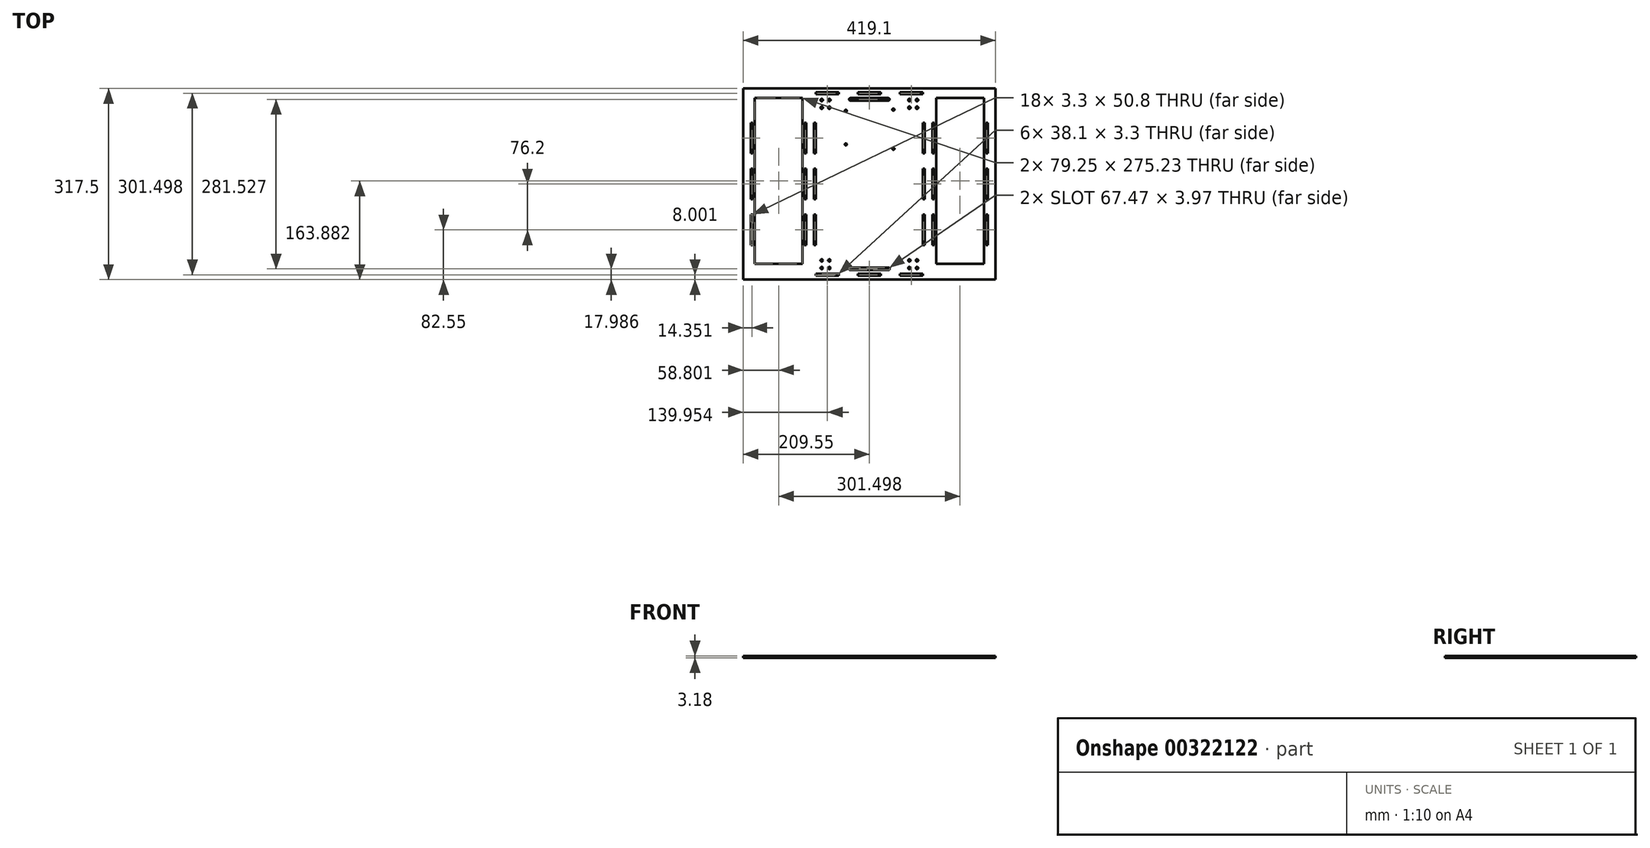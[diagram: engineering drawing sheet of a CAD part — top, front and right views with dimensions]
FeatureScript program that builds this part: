
annotation { "Feature Type Name" : "Feature", "Feature Type Description" : "" }
export const myFeature = defineFeature(function(context is Context, id is Id, definition is map)
    precondition{}
    {
        {
            var Q0;
            Q0=qCreatedBy(makeId("Top.planeOp"),FACE);
            var sketch = newSketch(context, id + "F0", { "sketchPlane" : qUnion([Q0])});
            skLineSegment(sketch, "E0.bottom", {"start": v(111.12, -158.75) * mm, "end": v(-111.12, -158.75) * mm});
            skLineSegment(sketch, "E0.top", {"start": v(111.12, 158.75) * mm, "end": v(-111.12, 158.75) * mm});
            skLineSegment(sketch, "E0.left", {"start": v(111.12, -158.75) * mm, "end": v(111.12, 158.75) * mm, "construction": true});
            skPoint(sketch, "E0.middle", {"position": v(0, 0) * mm});
            skLineSegment(sketch, "E1.bottom", {"start": v(-88.65, 152.4) * mm, "end": v(-50.55, 152.4) * mm});
            skLineSegment(sketch, "E1.top", {"start": v(-88.65, 149.1) * mm, "end": v(-50.55, 149.1) * mm});
            skLineSegment(sketch, "E1.left", {"start": v(-88.65, 152.4) * mm, "end": v(-88.65, 149.1) * mm});
            skLineSegment(sketch, "E1.right", {"start": v(-50.55, 152.4) * mm, "end": v(-50.55, 149.1) * mm});
            skLineSegment(sketch, "E2.bottom", {"start": v(-19.05, 152.4) * mm, "end": v(19.05, 152.4) * mm});
            skLineSegment(sketch, "E2.top", {"start": v(-19.05, 149.1) * mm, "end": v(19.05, 149.1) * mm});
            skLineSegment(sketch, "E2.left", {"start": v(-19.05, 152.4) * mm, "end": v(-19.05, 149.1) * mm});
            skLineSegment(sketch, "E2.right", {"start": v(19.05, 152.4) * mm, "end": v(19.05, 149.1) * mm});
            skLineSegment(sketch, "E3", {"start": v(-50.55, 152.4) * mm, "end": v(-19.05, 152.4) * mm, "construction": true});
            skLineSegment(sketch, "E4.MirrorCS", {"start": v(88.65, 149.1) * mm, "end": v(50.55, 149.1) * mm});
            skLineSegment(sketch, "E5.MirrorCS", {"start": v(88.65, 152.4) * mm, "end": v(50.55, 152.4) * mm});
            skLineSegment(sketch, "E6.MirrorCS", {"start": v(50.55, 152.4) * mm, "end": v(50.55, 149.1) * mm});
            skLineSegment(sketch, "E7.MirrorCS", {"start": v(88.65, 152.4) * mm, "end": v(88.65, 149.1) * mm});
            skLineSegment(sketch, "E8.MirrorCS", {"start": v(-50.55, -152.4) * mm, "end": v(-50.55, -149.1) * mm});
            skLineSegment(sketch, "E9.MirrorCS", {"start": v(-19.05, -149.1) * mm, "end": v(19.05, -149.1) * mm});
            skLineSegment(sketch, "E10.MirrorCS", {"start": v(19.05, -152.4) * mm, "end": v(19.05, -149.1) * mm});
            skLineSegment(sketch, "E11.MirrorCS", {"start": v(88.65, -149.1) * mm, "end": v(50.55, -149.1) * mm});
            skLineSegment(sketch, "E12.MirrorCS", {"start": v(50.55, -152.4) * mm, "end": v(50.55, -149.1) * mm});
            skLineSegment(sketch, "E13.MirrorCS", {"start": v(-88.65, -149.1) * mm, "end": v(-50.55, -149.1) * mm});
            skLineSegment(sketch, "E14.MirrorCS", {"start": v(88.65, -152.4) * mm, "end": v(88.65, -149.1) * mm});
            skLineSegment(sketch, "E15.MirrorCS", {"start": v(-19.05, -152.4) * mm, "end": v(-19.05, -149.1) * mm});
            skLineSegment(sketch, "E16.MirrorCS", {"start": v(88.65, -152.4) * mm, "end": v(50.55, -152.4) * mm});
            skLineSegment(sketch, "E17.MirrorCS", {"start": v(-19.05, -152.4) * mm, "end": v(19.05, -152.4) * mm});
            skLineSegment(sketch, "E18.MirrorCS", {"start": v(-50.55, -152.4) * mm, "end": v(-19.05, -152.4) * mm, "construction": true});
            skLineSegment(sketch, "E19.MirrorCS", {"start": v(-88.65, -152.4) * mm, "end": v(-50.55, -152.4) * mm});
            skLineSegment(sketch, "E20.MirrorCS", {"start": v(-88.65, -152.4) * mm, "end": v(-88.65, -149.1) * mm});
            skLineSegment(sketch, "E21.bottom", {"start": v(-107.95, 101.6) * mm, "end": v(-104.65, 101.6) * mm});
            skLineSegment(sketch, "E21.top", {"start": v(-107.95, 50.8) * mm, "end": v(-104.65, 50.8) * mm});
            skLineSegment(sketch, "E21.left", {"start": v(-107.95, 101.6) * mm, "end": v(-107.95, 50.8) * mm});
            skLineSegment(sketch, "E21.right", {"start": v(-104.65, 101.6) * mm, "end": v(-104.65, 50.8) * mm});
            skLineSegment(sketch, "E22.0.1.0", {"start": v(-104.65, 25.4) * mm, "end": v(-104.65, -25.4) * mm});
            skLineSegment(sketch, "E22.0.1.1", {"start": v(-107.95, 25.4) * mm, "end": v(-107.95, -25.4) * mm});
            skLineSegment(sketch, "E22.0.1.2", {"start": v(-107.95, 25.4) * mm, "end": v(-104.65, 25.4) * mm});
            skLineSegment(sketch, "E22.0.1.3", {"start": v(-107.95, -25.4) * mm, "end": v(-104.65, -25.4) * mm});
            skLineSegment(sketch, "E22.0.2.0", {"start": v(-104.65, -50.8) * mm, "end": v(-104.65, -101.6) * mm});
            skLineSegment(sketch, "E22.0.2.1", {"start": v(-107.95, -50.8) * mm, "end": v(-107.95, -101.6) * mm});
            skLineSegment(sketch, "E22.0.2.2", {"start": v(-107.95, -50.8) * mm, "end": v(-104.65, -50.8) * mm});
            skLineSegment(sketch, "E22.0.2.3", {"start": v(-107.95, -101.6) * mm, "end": v(-104.65, -101.6) * mm});
            skLineSegment(sketch, "E22.direction1", {"start": v(-107.95, 50.8) * mm, "end": v(-91.95, 50.8) * mm, "construction": true});
            skLineSegment(sketch, "E22.direction2", {"start": v(-107.95, 50.8) * mm, "end": v(-107.95, -25.4) * mm, "construction": true});
            skLineSegment(sketch, "E23.MirrorCS", {"start": v(104.65, 25.4) * mm, "end": v(104.65, -25.4) * mm});
            skLineSegment(sketch, "E24.MirrorCS", {"start": v(107.95, -50.8) * mm, "end": v(104.65, -50.8) * mm});
            skLineSegment(sketch, "E25.MirrorCS", {"start": v(107.95, 25.4) * mm, "end": v(107.95, -25.4) * mm});
            skLineSegment(sketch, "E26.MirrorCS", {"start": v(107.95, -101.6) * mm, "end": v(104.65, -101.6) * mm});
            skLineSegment(sketch, "E27.MirrorCS", {"start": v(107.95, 25.4) * mm, "end": v(104.65, 25.4) * mm});
            skLineSegment(sketch, "E28.MirrorCS", {"start": v(107.95, -25.4) * mm, "end": v(104.65, -25.4) * mm});
            skLineSegment(sketch, "E29.MirrorCS", {"start": v(107.95, 50.8) * mm, "end": v(107.95, -25.4) * mm, "construction": true});
            skLineSegment(sketch, "E30.MirrorCS", {"start": v(107.95, 101.6) * mm, "end": v(104.65, 101.6) * mm});
            skLineSegment(sketch, "E31.MirrorCS", {"start": v(107.95, 50.8) * mm, "end": v(104.65, 50.8) * mm});
            skLineSegment(sketch, "E32.MirrorCS", {"start": v(107.95, 101.6) * mm, "end": v(107.95, 50.8) * mm});
            skLineSegment(sketch, "E33.MirrorCS", {"start": v(104.65, -50.8) * mm, "end": v(104.65, -101.6) * mm});
            skLineSegment(sketch, "E34.MirrorCS", {"start": v(104.65, 101.6) * mm, "end": v(104.65, 50.8) * mm});
            skLineSegment(sketch, "E35.MirrorCS", {"start": v(107.95, -50.8) * mm, "end": v(107.95, -101.6) * mm});
            skPoint(sketch, "E36.middle", {"position": v(0, 93.75) * mm});
            skCircle(sketch, "E37", {"center": v(39.92, 123.7) * mm, "radius": 1.75 * mm});
            skCircle(sketch, "E38", {"center": v(39.92, 58.7) * mm, "radius": 1.75 * mm});
            skCircle(sketch, "E39", {"center": v(-39.04, 65.88) * mm, "radius": 1.75 * mm});
            skCircle(sketch, "E40.MirrorC", {"center": v(-39.04, 121.62) * mm, "radius": 1.75 * mm});
            skLineSegment(sketch, "E41.0.1.0", {"start": v(-88.65, 101.6) * mm, "end": v(-88.65, 50.8) * mm});
            skLineSegment(sketch, "E41.3.1.0", {"start": v(-91.95, 101.6) * mm, "end": v(-91.95, 50.8) * mm});
            skLineSegment(sketch, "E41.6.1.0", {"start": v(-91.95, 101.6) * mm, "end": v(-88.65, 101.6) * mm});
            skLineSegment(sketch, "E41.9.1.0", {"start": v(-91.95, 50.8) * mm, "end": v(-88.65, 50.8) * mm});
            skLineSegment(sketch, "E41.0.1.1", {"start": v(-88.65, 25.4) * mm, "end": v(-88.65, -25.4) * mm});
            skLineSegment(sketch, "E41.3.1.1", {"start": v(-91.95, 25.4) * mm, "end": v(-91.95, -25.4) * mm});
            skLineSegment(sketch, "E41.6.1.1", {"start": v(-91.95, 25.4) * mm, "end": v(-88.65, 25.4) * mm});
            skLineSegment(sketch, "E41.9.1.1", {"start": v(-91.95, -25.4) * mm, "end": v(-88.65, -25.4) * mm});
            skLineSegment(sketch, "E41.0.1.2", {"start": v(-88.65, -50.8) * mm, "end": v(-88.65, -101.6) * mm});
            skLineSegment(sketch, "E41.3.1.2", {"start": v(-91.95, -50.8) * mm, "end": v(-91.95, -101.6) * mm});
            skLineSegment(sketch, "E41.6.1.2", {"start": v(-91.95, -50.8) * mm, "end": v(-88.65, -50.8) * mm});
            skLineSegment(sketch, "E41.9.1.2", {"start": v(-91.95, -101.6) * mm, "end": v(-88.65, -101.6) * mm});
            skLineSegment(sketch, "E42.MirrorCS", {"start": v(91.95, 101.6) * mm, "end": v(91.95, 50.8) * mm});
            skLineSegment(sketch, "E43.MirrorCS", {"start": v(91.95, 101.6) * mm, "end": v(88.65, 101.6) * mm});
            skLineSegment(sketch, "E44.MirrorCS", {"start": v(91.95, 50.8) * mm, "end": v(88.65, 50.8) * mm});
            skLineSegment(sketch, "E45.MirrorCS", {"start": v(91.95, -50.8) * mm, "end": v(91.95, -101.6) * mm});
            skLineSegment(sketch, "E46.MirrorCS", {"start": v(88.65, 25.4) * mm, "end": v(88.65, -25.4) * mm});
            skLineSegment(sketch, "E47.MirrorCS", {"start": v(91.95, -50.8) * mm, "end": v(88.65, -50.8) * mm});
            skLineSegment(sketch, "E48.MirrorCS", {"start": v(91.95, 25.4) * mm, "end": v(91.95, -25.4) * mm});
            skLineSegment(sketch, "E49.MirrorCS", {"start": v(91.95, -101.6) * mm, "end": v(88.65, -101.6) * mm});
            skLineSegment(sketch, "E50.MirrorCS", {"start": v(91.95, 25.4) * mm, "end": v(88.65, 25.4) * mm});
            skLineSegment(sketch, "E51.MirrorCS", {"start": v(91.95, -25.4) * mm, "end": v(88.65, -25.4) * mm});
            skLineSegment(sketch, "E52.MirrorCS", {"start": v(88.65, 101.6) * mm, "end": v(88.65, 50.8) * mm});
            skLineSegment(sketch, "E53.MirrorCS", {"start": v(88.65, -50.8) * mm, "end": v(88.65, -101.6) * mm});
            skLineSegment(sketch, "E54", {"start": v(-88.65, 101.6) * mm, "end": v(-88.65, 149.1) * mm, "construction": true});
            skCircle(sketch, "E55", {"center": v(-79.12, 139.57) * mm, "radius": 1.98 * mm});
            skCircle(sketch, "E56", {"center": v(-66.42, 139.57) * mm, "radius": 1.98 * mm});
            skCircle(sketch, "E57", {"center": v(-79.12, 126.87) * mm, "radius": 1.98 * mm});
            skCircle(sketch, "E58", {"center": v(-66.42, 126.87) * mm, "radius": 1.98 * mm});
            skCircle(sketch, "E59.MirrorC", {"center": v(79.12, 126.87) * mm, "radius": 1.98 * mm});
            skCircle(sketch, "E60.MirrorC", {"center": v(79.12, 139.57) * mm, "radius": 1.98 * mm});
            skCircle(sketch, "E61.MirrorC", {"center": v(66.42, 139.57) * mm, "radius": 1.98 * mm});
            skCircle(sketch, "E62.MirrorC", {"center": v(66.42, 126.87) * mm, "radius": 1.98 * mm});
            skCircle(sketch, "E63.MirrorC", {"center": v(-79.12, -139.57) * mm, "radius": 1.98 * mm});
            skCircle(sketch, "E64.MirrorC", {"center": v(-79.12, -126.87) * mm, "radius": 1.98 * mm});
            skCircle(sketch, "E65.MirrorC", {"center": v(-66.42, -139.57) * mm, "radius": 1.98 * mm});
            skCircle(sketch, "E66.MirrorC", {"center": v(-66.42, -126.87) * mm, "radius": 1.98 * mm});
            skCircle(sketch, "E67.MirrorC", {"center": v(66.42, -139.57) * mm, "radius": 1.98 * mm});
            skCircle(sketch, "E68.MirrorC", {"center": v(79.12, -126.87) * mm, "radius": 1.98 * mm});
            skCircle(sketch, "E69.MirrorC", {"center": v(66.42, -126.87) * mm, "radius": 1.98 * mm});
            skCircle(sketch, "E70.MirrorC", {"center": v(79.12, -139.57) * mm, "radius": 1.98 * mm});
            skLineSegment(sketch, "E71.bottom", {"start": v(228.6, -228.6) * mm, "end": v(-228.6, -228.6) * mm, "construction": true});
            skLineSegment(sketch, "E71.top", {"start": v(228.6, 228.6) * mm, "end": v(-228.6, 228.6) * mm, "construction": true});
            skLineSegment(sketch, "E71.left", {"start": v(228.6, -228.6) * mm, "end": v(228.6, 228.6) * mm, "construction": true});
            skLineSegment(sketch, "E71.right", {"start": v(-228.6, -228.6) * mm, "end": v(-228.6, 228.6) * mm, "construction": true});
            skLineSegment(sketch, "E72", {"start": v(111.12, 158.75) * mm, "end": v(209.55, 158.75) * mm});
            skLineSegment(sketch, "E73", {"start": v(209.55, 158.75) * mm, "end": v(209.55, -158.75) * mm});
            skLineSegment(sketch, "E74", {"start": v(209.55, -158.75) * mm, "end": v(111.12, -158.75) * mm});
            skLineSegment(sketch, "E75.bottom", {"start": v(111.12, 142.75) * mm, "end": v(190.37, 142.75) * mm});
            skLineSegment(sketch, "E75.top", {"start": v(111.12, -132.48) * mm, "end": v(190.37, -132.48) * mm});
            skLineSegment(sketch, "E75.left", {"start": v(111.12, 142.75) * mm, "end": v(111.12, -132.48) * mm});
            skLineSegment(sketch, "E75.right", {"start": v(190.37, 142.75) * mm, "end": v(190.37, -132.48) * mm});
            skLineSegment(sketch, "E76.1.0.0", {"start": v(196.85, -25.4) * mm, "end": v(193.55, -25.4) * mm});
            skLineSegment(sketch, "E76.1.0.1", {"start": v(193.55, -50.8) * mm, "end": v(193.55, -101.6) * mm});
            skLineSegment(sketch, "E76.1.0.2", {"start": v(196.85, 101.6) * mm, "end": v(196.85, 50.8) * mm});
            skLineSegment(sketch, "E76.1.0.3", {"start": v(196.85, 50.8) * mm, "end": v(193.55, 50.8) * mm});
            skLineSegment(sketch, "E76.1.0.4", {"start": v(196.85, 25.4) * mm, "end": v(193.55, 25.4) * mm});
            skLineSegment(sketch, "E76.1.0.5", {"start": v(196.85, 50.8) * mm, "end": v(196.85, -25.4) * mm, "construction": true});
            skLineSegment(sketch, "E76.1.0.6", {"start": v(193.55, 25.4) * mm, "end": v(193.55, -25.4) * mm});
            skLineSegment(sketch, "E76.1.0.7", {"start": v(193.55, 101.6) * mm, "end": v(193.55, 50.8) * mm});
            skLineSegment(sketch, "E76.1.0.8", {"start": v(196.85, 25.4) * mm, "end": v(196.85, -25.4) * mm});
            skLineSegment(sketch, "E76.1.0.9", {"start": v(196.85, -50.8) * mm, "end": v(193.55, -50.8) * mm});
            skLineSegment(sketch, "E76.1.0.10", {"start": v(196.85, -101.6) * mm, "end": v(193.55, -101.6) * mm});
            skLineSegment(sketch, "E76.1.0.11", {"start": v(196.85, -50.8) * mm, "end": v(196.85, -101.6) * mm});
            skLineSegment(sketch, "E76.1.0.12", {"start": v(196.85, 101.6) * mm, "end": v(193.55, 101.6) * mm});
            skLineSegment(sketch, "E76.direction1", {"start": v(104.65, -101.6) * mm, "end": v(193.55, -101.6) * mm, "construction": true});
            skLineSegment(sketch, "E77.MirrorCS", {"start": v(-196.85, 50.8) * mm, "end": v(-196.85, -25.4) * mm, "construction": true});
            skLineSegment(sketch, "E78.MirrorCS", {"start": v(-196.85, -101.6) * mm, "end": v(-193.55, -101.6) * mm});
            skLineSegment(sketch, "E79.MirrorCS", {"start": v(-111.12, -158.75) * mm, "end": v(-111.12, 158.75) * mm, "construction": true});
            skLineSegment(sketch, "E80.MirrorCS", {"start": v(-196.85, 101.6) * mm, "end": v(-193.55, 101.6) * mm});
            skLineSegment(sketch, "E81.MirrorCS", {"start": v(-193.55, -50.8) * mm, "end": v(-193.55, -101.6) * mm});
            skLineSegment(sketch, "E82.MirrorCS", {"start": v(-193.55, 101.6) * mm, "end": v(-193.55, 50.8) * mm});
            skLineSegment(sketch, "E83.MirrorCS", {"start": v(-111.12, 158.75) * mm, "end": v(-209.55, 158.75) * mm});
            skLineSegment(sketch, "E84.MirrorCS", {"start": v(-196.85, 50.8) * mm, "end": v(-193.55, 50.8) * mm});
            skLineSegment(sketch, "E85.MirrorCS", {"start": v(-209.55, -158.75) * mm, "end": v(-111.12, -158.75) * mm});
            skLineSegment(sketch, "E86.MirrorCS", {"start": v(-196.85, -50.8) * mm, "end": v(-193.55, -50.8) * mm});
            skLineSegment(sketch, "E87.MirrorCS", {"start": v(-196.85, -50.8) * mm, "end": v(-196.85, -101.6) * mm});
            skLineSegment(sketch, "E88.MirrorCS", {"start": v(-196.85, -25.4) * mm, "end": v(-193.55, -25.4) * mm});
            skLineSegment(sketch, "E89.MirrorCS", {"start": v(-111.12, -132.48) * mm, "end": v(-190.37, -132.48) * mm});
            skLineSegment(sketch, "E90.MirrorCS", {"start": v(-193.55, 25.4) * mm, "end": v(-193.55, -25.4) * mm});
            skLineSegment(sketch, "E91.MirrorCS", {"start": v(-196.85, 101.6) * mm, "end": v(-196.85, 50.8) * mm});
            skLineSegment(sketch, "E92.MirrorCS", {"start": v(-196.85, 25.4) * mm, "end": v(-196.85, -25.4) * mm});
            skLineSegment(sketch, "E93.MirrorCS", {"start": v(-209.55, 158.75) * mm, "end": v(-209.55, -158.75) * mm});
            skLineSegment(sketch, "E94.MirrorCS", {"start": v(-190.37, 142.75) * mm, "end": v(-190.37, -132.48) * mm});
            skLineSegment(sketch, "E95.MirrorCS", {"start": v(-196.85, 25.4) * mm, "end": v(-193.55, 25.4) * mm});
            skLineSegment(sketch, "E96.MirrorCS", {"start": v(-111.12, 142.75) * mm, "end": v(-190.37, 142.75) * mm});
            skLineSegment(sketch, "E97", {"start": v(-111.12, 142.75) * mm, "end": v(-111.12, -132.48) * mm});
            skPoint(sketch, "E98", {"position": v(0, 149.1) * mm});
            skLineSegment(sketch, "E99", {"start": v(0, 142.75) * mm, "end": v(-31.75, 142.75) * mm});
            skArc(sketch, "E100", {"start": v(-31.75, 142.75) * mm, "mid": v(-33.73, 140.76) * mm, "end": v(-31.75, 138.78) * mm});
            skLineSegment(sketch, "E101", {"start": v(-31.75, 138.78) * mm, "end": v(0, 138.78) * mm});
            skLineSegment(sketch, "E102.MirrorCS", {"start": v(0, 142.75) * mm, "end": v(31.75, 142.75) * mm});
            skArc(sketch, "E103.MirrorCS", {"start": v(31.75, 142.75) * mm, "mid": v(33.73, 140.76) * mm, "end": v(31.75, 138.78) * mm});
            skLineSegment(sketch, "E104.MirrorCS", {"start": v(31.75, 138.78) * mm, "end": v(0, 138.78) * mm});
            skLineSegment(sketch, "E105.MirrorCS", {"start": v(-31.75, -138.78) * mm, "end": v(0, -138.78) * mm});
            skLineSegment(sketch, "E106.MirrorCS", {"start": v(31.75, -138.78) * mm, "end": v(0, -138.78) * mm});
            skLineSegment(sketch, "E107.MirrorCS", {"start": v(0, -142.75) * mm, "end": v(31.75, -142.75) * mm});
            skLineSegment(sketch, "E108.MirrorCS", {"start": v(0, -142.75) * mm, "end": v(-31.75, -142.75) * mm});
            skArc(sketch, "E109.MirrorCS", {"start": v(-31.75, -142.75) * mm, "mid": v(-33.73, -140.76) * mm, "end": v(-31.75, -138.78) * mm});
            skArc(sketch, "E110.MirrorCS", {"start": v(31.75, -142.75) * mm, "mid": v(33.73, -140.76) * mm, "end": v(31.75, -138.78) * mm});
            skSolve(sketch);
        }
        {
            var Q0;
            Q0=makeQuery(id+"F0.imprint","IMPRINT",FACE,{"disambiguationData":[TD([[makeQuery(id+"F0.imprint","IMPRINT",EDGE,{"derivedFrom":sQuery(id+"F0.wireOp",EDGE,"E0.bottom")}),-1.0]])]});
            extrude(context, id + "F1", {"entities" : qUnion([Q0]), "depth" : 3.17 * mm});
        }
    });
